# Revit family: PRD_AR_CntrTpWshBsns_RONDATopCountertopWashbasin_ANMT2001
name_source: partatom
category: Plumbing Fixtures
revit_build: Autodesk Revit 2018 (Build: 20190510_1515(x64)
units: mm (PartAtom-declared; Revit-internal decimal feet)

## family parameters
Cut with Voids When Loaded = No
Host = Face
OmniClass Number = 23.45.05.14.14
OmniClass Title = Sinks/Lavatories
Part Type = Normal
Room Calculation Point = No
Round Connector Dimension = Use Diameter
Shared = No

## types (1)
- ANMT2001
    AssetType = Fixed
    BIMObjectName = PRD_AR_CounterTopWashBasins_RONDATopCountertopWashbasin_ANMT2001
    BowlDepth = 355.00 mm
    BowlHeight = 100.00 mm
    BowlShape = Circle
    BowlWidth = 355.00 mm
    Category = Pr_40_20_96_18, Countertop washbasins
    Color = alpine white
    Default Elevation = 850 mm  [stored 2.78871 ft]
    Description = RONDAtop countertop basin, made of MIRANIT resin-bonded mineral material with pore-free, alpine white smooth surface (temperature-resistant up to 80°C). Round shape with seamless bowl, without overflow. No silicone sealant is required due to the invisible seal which is integrated in to the mounting edge. Drilling templates and mounting materials included. Bowl dimensions 355 x 100 mm (W x H).
    DiameterNominal = 32 mm
    DrainSize = 32 mm  [stored 0.104987 ft]
    DurationUnit = year
    Features = mineral material, alpine white smooth surface, round shape
    Finish = smooth
    Flow = 0.0 L/s
    GrossWeight = 11.50 kg
    IfcExportAs = IfcSanitaryTerminalType
    IfcExportType = WASHHANDBASIN
    IntegralAccessories = incl. drilling templates and mounting materials
    Manufacturer = KWC Group AG
    ManufacturerName = KWC Group AG
    ManufacturerURL = www.kwc.com
    Material = mineral material
    MaterialCode = Miranit
    Model = ANMT2001
    ModelNumber = 2030054380
    ModelReference = ANMT2001
    MountingOffset = 140 mm  [stored 0.459318 ft]
    NBSDescription = Counter top wash basins
    NBSReference = 45-35-70/360
    Name = Countertop Washbasin ANMT2001
    NetWeight = 9.50 kg
    NominalDepth = 370 mm  [stored 1.21391 ft]
    NominalHeight = 140 mm  [stored 0.459318 ft]
    NominalWidth = 370 mm  [stored 1.21391 ft]
    NumberOfBowls = 1
    Overflow = No
    ProductInformation = https://pim.kwc.com
    Shape = round
    SiphonIncluded = No
    Size = 370 x 140 mm (W x H)
    Spillway = No
    Splashback = No
    TailorMade = No
    TapLedge = No
    TypeOfBasin = Vanity basin
    TypeOfMounting = Table mounting
    URL = www.kwc.com
    Uniclass2015Code = Pr_40_20_96_18
    Uniclass2015Title = Countertop washbasins
    Uniclass2015Version = Products v1.17
    Version = 1
    WarrantyDurationUnit = year
    WashbasinMaterial = PRD_AR_Miranit_Alpinewhite
    WasteHolePosition = Center
    WasteHoleProjection = 150.00 mm
    WasteKitIncluded = No
    WasteSize = DN 32

note: [stored X ft] marks values corroborated as IEEE doubles in the binary element streams (Revit-internal decimal feet)

## geometry (parser evidence)
native form markers: Sweep x7
no freeform markers — native parametric forms only
